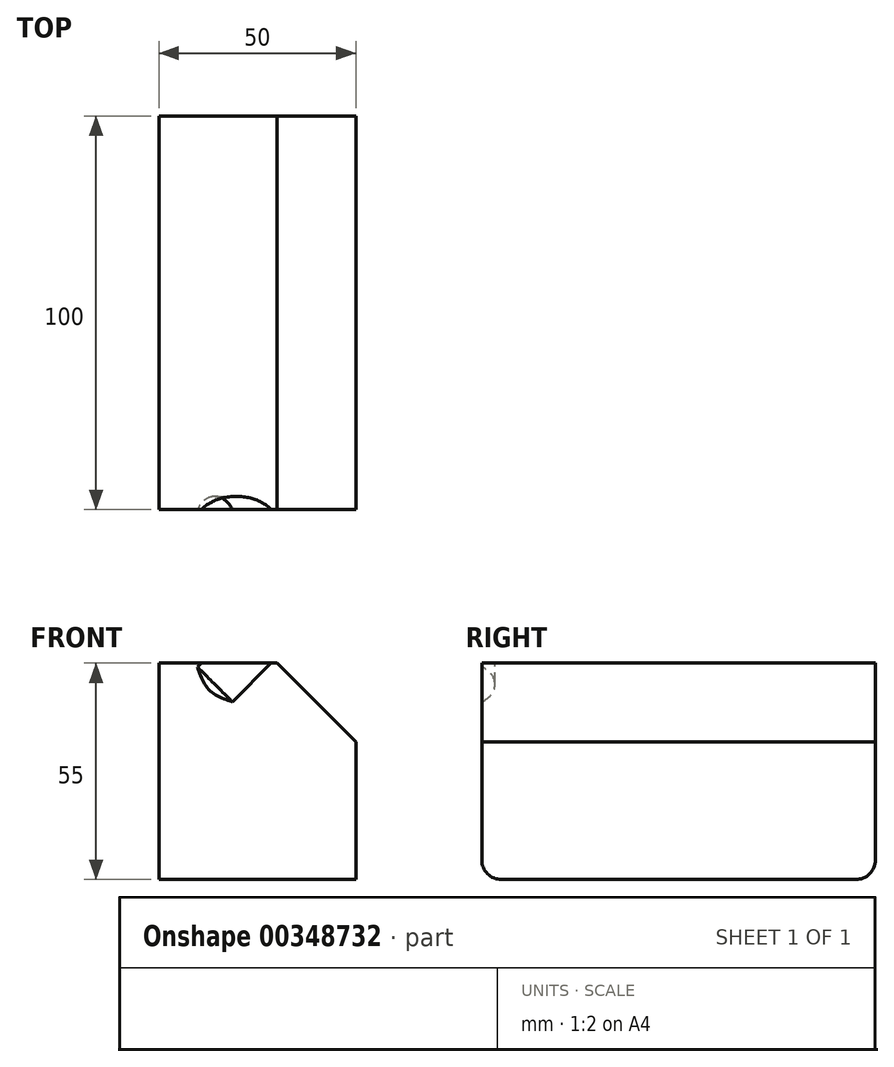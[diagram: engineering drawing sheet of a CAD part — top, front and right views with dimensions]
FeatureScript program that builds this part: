
annotation { "Feature Type Name" : "Feature", "Feature Type Description" : "" }
export const myFeature = defineFeature(function(context is Context, id is Id, definition is map)
    precondition{}
    {
        {
            var Q0;
            Q0=qCreatedBy(makeId("Top.planeOp"),FACE);
            var sketch = newSketch(context, id + "F0", { "sketchPlane" : qUnion([Q0])});
            skLineSegment(sketch, "E0.bottom", {"start": v(0, 0) * mm, "end": v(50, 0) * mm});
            skLineSegment(sketch, "E0.top", {"start": v(0, 100) * mm, "end": v(50, 100) * mm});
            skLineSegment(sketch, "E0.left", {"start": v(0, 0) * mm, "end": v(0, 100) * mm});
            skLineSegment(sketch, "E0.right", {"start": v(50, 0) * mm, "end": v(50, 100) * mm});
            skSolve(sketch);
        }
        {
            var Q0;
            Q0 = qSketchRegion(id + "F0", true);
            extrude(context, id + "F1", {"entities" : qUnion([Q0]), "depth" : 55 * mm});
        }
        {
            var Q0;
            Q0=makeQuery(id+"F1.opExtrude","CAP_EDGE",EDGE,{"disambiguationData":[OSD([sQuery(id+"F0.wireOp",EDGE,"E0.right")])],"isStart":false});
            chamfer(context, id + "F2", {"entities" : qUnion([Q0]), "width" : 20 * mm, "tangentPropagation" : true});
        }
        {
            var Q0;
            Q0=makeQuery(id+"F2.opChamfer","BLEND_FACE",FACE,{"disambiguationData":[OSD([sQuery(id+"F0.wireOp",EDGE,"E0.right")])]});
            var sketch = newSketch(context, id + "F3", { "sketchPlane" : qUnion([Q0])});
            skPoint(sketch, "E1", {"position": v(-4.14, 25) * mm});
            skPoint(sketch, "E2", {"position": v(-4.14, 75.6) * mm});
            skSolve(sketch);
        }
        {
            var Q0;
            Q0=sQuery(id+"F3.wireOp",VERTEX,"E1");
            var Q1;
            Q1=makeQuery(id+"F1.opExtrude","SWEPT_BODY",BODY,{"disambiguationData":[OSD([sQuery(id+"F0.wireOp",EDGE,"E0.bottom"),sQuery(id+"F0.wireOp",EDGE,"E0.top"),sQuery(id+"F0.wireOp",EDGE,"E0.left"),sQuery(id+"F0.wireOp",EDGE,"E0.right")])]});
            hole(context, id + "F4", {"style" : HoleStyle.SIMPLE, "endStyle" : HoleEndStyle.BLIND, "holeDiameter" : 15 * mm, "holeDepth" : 15 * mm, "isTappedThrough" : true, "tappedDepth" : 12 * mm, "tapClearance" : 3, "startFromSketch" : true, "locations" : qUnion([Q0]), "scope" : qUnion([Q1])});
        }
        {
            var Q0;
            Q0=makeQuery(id+"F2.opChamfer","BLEND_FACE",FACE,{"disambiguationData":[OSD([sQuery(id+"F0.wireOp",EDGE,"E0.right")])]});
            var sketch = newSketch(context, id + "F5", { "sketchPlane" : qUnion([Q0])});
            skPoint(sketch, "E3", {"position": v(-3.94, 75) * mm});
            skSolve(sketch);
        }
        {
            var Q0;
            Q0=sQuery(id+"F5.wireOp",VERTEX,"E3");
            var Q1;
            Q1=makeQuery(id+"F1.opExtrude","SWEPT_BODY",BODY,{"disambiguationData":[OSD([sQuery(id+"F0.wireOp",EDGE,"E0.bottom"),sQuery(id+"F0.wireOp",EDGE,"E0.top"),sQuery(id+"F0.wireOp",EDGE,"E0.left"),sQuery(id+"F0.wireOp",EDGE,"E0.right")])]});
            hole(context, id + "F6", {"style" : HoleStyle.SIMPLE, "endStyle" : HoleEndStyle.BLIND, "holeDiameter" : 15 * mm, "holeDepth" : 15 * mm, "isTappedThrough" : true, "tappedDepth" : 12 * mm, "tapClearance" : 3, "startFromSketch" : true, "locations" : qUnion([Q0]), "scope" : qUnion([Q1])});
        }
        {
            var Q0;
            Q0=makeQuery(id+"F2.opChamfer","BLEND_FACE",FACE,{"disambiguationData":[OSD([sQuery(id+"F0.wireOp",EDGE,"E0.right")])]});
            var sketch = newSketch(context, id + "F7", { "sketchPlane" : qUnion([Q0])});
            skSolve(sketch);
        }
        {
            var Q0;
            Q0=makeQuery(id+"F1.opExtrude","CAP_EDGE",EDGE,{"disambiguationData":[OSD([sQuery(id+"F0.wireOp",EDGE,"E0.top")])],"isStart":true});
            fillet(context, id + "F8", {"entities" : qUnion([Q0]), "radius" : 5 * mm, "tangentPropagation" : true, "allowEdgeOverflow" : false});
        }
        {
            var Q0;
            Q0=makeQuery(id+"F1.opExtrude","CAP_EDGE",EDGE,{"disambiguationData":[OSD([sQuery(id+"F0.wireOp",EDGE,"E0.bottom")])],"isStart":true});
            fillet(context, id + "F9", {"entities" : qUnion([Q0]), "radius" : 5 * mm, "tangentPropagation" : true, "allowEdgeOverflow" : false});
        }
    });
